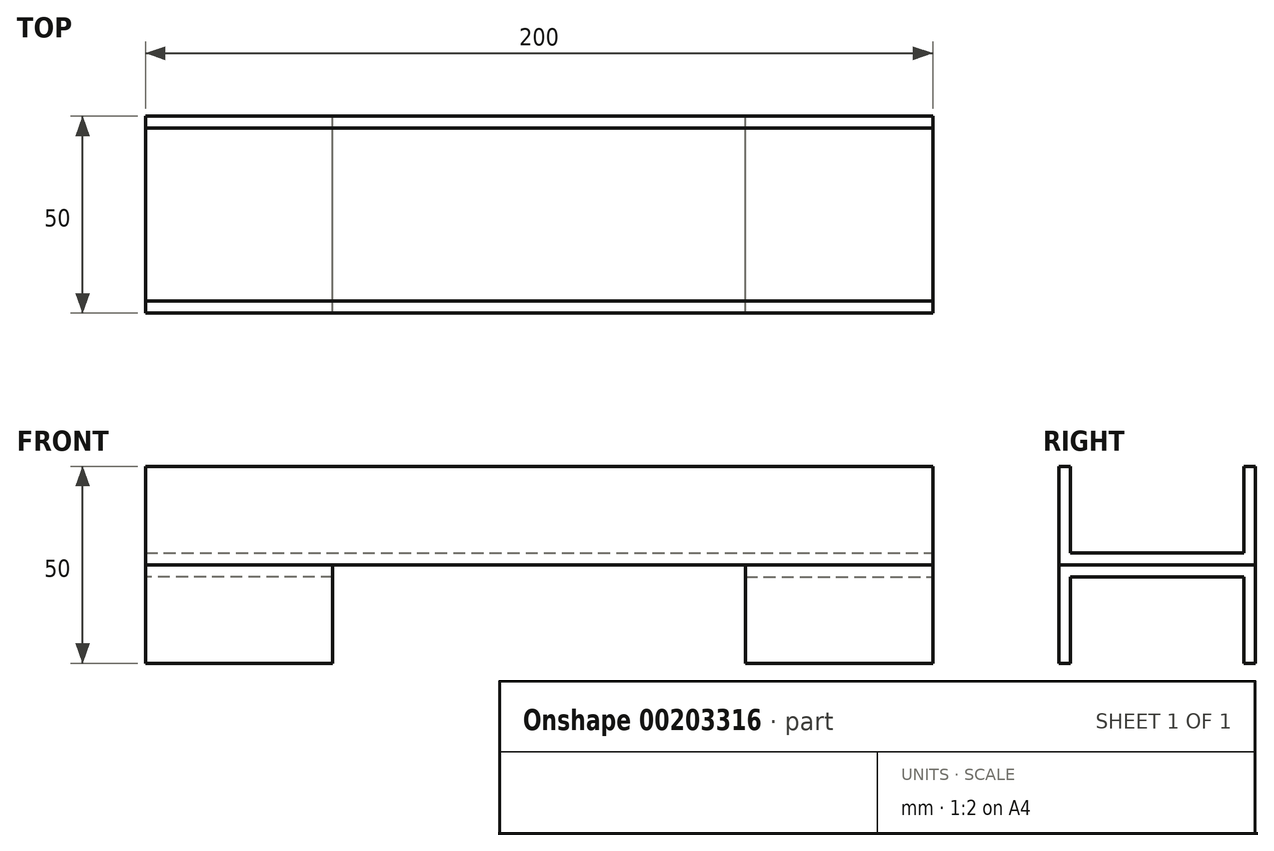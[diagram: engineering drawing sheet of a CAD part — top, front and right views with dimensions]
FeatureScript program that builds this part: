
annotation { "Feature Type Name" : "Feature", "Feature Type Description" : "" }
export const myFeature = defineFeature(function(context is Context, id is Id, definition is map)
    precondition{}
    {
        {
            var Q0;
            Q0=qCreatedBy(makeId("Front.planeOp"),FACE);
            var sketch = newSketch(context, id + "F0", { "sketchPlane" : qUnion([Q0])});
            skLineSegment(sketch, "E0.bottom", {"start": v(100, -12.5) * mm, "end": v(-100, -12.5) * mm});
            skLineSegment(sketch, "E0.top", {"start": v(100, 12.5) * mm, "end": v(-100, 12.5) * mm});
            skLineSegment(sketch, "E0.left", {"start": v(100, -12.5) * mm, "end": v(100, 12.5) * mm});
            skLineSegment(sketch, "E0.right", {"start": v(-100, -12.5) * mm, "end": v(-100, 12.5) * mm});
            skPoint(sketch, "E0.middle", {"position": v(0, 0) * mm});
            skSolve(sketch);
        }
        {
            var Q0;
            Q0 = qSketchRegion(id + "F0", true);
            extrude(context, id + "F1", {"entities" : qUnion([Q0]), "depth" : 50 * mm});
        }
        {
            var Q0;
            Q0=makeQuery(id+"F1.opExtrude","SWEPT_FACE",FACE,{"disambiguationData":[OSD([sQuery(id+"F0.wireOp",EDGE,"E0.left")])]});
            var sketch = newSketch(context, id + "F2", { "sketchPlane" : qUnion([Q0])});
            skLineSegment(sketch, "E1.bottom", {"start": v(-47, 12.5) * mm, "end": v(-3, 12.5) * mm});
            skLineSegment(sketch, "E1.top", {"start": v(-47, -9.5) * mm, "end": v(-3, -9.5) * mm});
            skLineSegment(sketch, "E1.left", {"start": v(-47, 12.5) * mm, "end": v(-47, -9.5) * mm});
            skLineSegment(sketch, "E1.right", {"start": v(-3, 12.5) * mm, "end": v(-3, -9.5) * mm});
            skLineSegment(sketch, "E2", {"start": v(-47, 6.87) * mm, "end": v(-50, 6.87) * mm, "construction": true});
            skLineSegment(sketch, "E3", {"start": v(-12.24, -9.5) * mm, "end": v(-12.24, -12.5) * mm, "construction": true});
            skLineSegment(sketch, "E4", {"start": v(-3, 5.6) * mm, "end": v(0, 5.6) * mm, "construction": true});
            skSolve(sketch);
        }
        {
            var Q0;
            Q0 = qSketchRegion(id + "F2", true);
            extrude(context, id + "F3", {"entities" : qUnion([Q0]), "operationType" : NewBodyOperationType.REMOVE, "endBound" : BoundingType.THROUGH_ALL, "oppositeDirection" : true, "depth" : 25 * mm});
        }
        {
            var Q0;
            Q0=makeQuery(id+"F1.opExtrude","SWEPT_FACE",FACE,{"disambiguationData":[OSD([sQuery(id+"F0.wireOp",EDGE,"E0.bottom")])]});
            var sketch = newSketch(context, id + "F4", { "sketchPlane" : qUnion([Q0])});
            skLineSegment(sketch, "E5.bottom", {"start": v(-100, 50) * mm, "end": v(-52.45, 50) * mm});
            skLineSegment(sketch, "E5.top", {"start": v(-100, 0) * mm, "end": v(-52.45, 0) * mm});
            skLineSegment(sketch, "E5.left", {"start": v(-100, 50) * mm, "end": v(-100, 0) * mm});
            skLineSegment(sketch, "E5.right", {"start": v(-52.45, 50) * mm, "end": v(-52.45, 0) * mm});
            skSolve(sketch);
        }
        {
            var Q0;
            Q0 = qSketchRegion(id + "F4", true);
            extrude(context, id + "F5", {"entities" : qUnion([Q0]), "depth" : 25 * mm});
        }
        {
            var Q0;
            Q0=makeQuery(id+"F5.opExtrude","SWEPT_FACE",FACE,{"disambiguationData":[OSD([sQuery(id+"F4.wireOp",EDGE,"E5.left")])]});
            var sketch = newSketch(context, id + "F6", { "sketchPlane" : qUnion([Q0])});
            skLineSegment(sketch, "E6.bottom", {"start": v(3, -37.5) * mm, "end": v(47, -37.5) * mm});
            skLineSegment(sketch, "E6.top", {"start": v(3, -15.5) * mm, "end": v(47, -15.5) * mm});
            skLineSegment(sketch, "E6.left", {"start": v(3, -37.5) * mm, "end": v(3, -15.5) * mm});
            skLineSegment(sketch, "E6.right", {"start": v(47, -37.5) * mm, "end": v(47, -15.5) * mm});
            skLineSegment(sketch, "E7", {"start": v(25, -15.5) * mm, "end": v(25, -12.5) * mm, "construction": true});
            skPoint(sketch, "E7.startSnap0", {"position": v(25, -12.5) * mm});
            skLineSegment(sketch, "E8", {"start": v(47, -26.5) * mm, "end": v(50, -26.5) * mm, "construction": true});
            skLineSegment(sketch, "E9", {"start": v(3, -26.5) * mm, "end": v(0, -26.5) * mm, "construction": true});
            skSolve(sketch);
        }
        {
            var Q0;
            Q0=makeQuery(id+"F6.imprint","IMPRINT",FACE,{"disambiguationData":[TD([[makeQuery(id+"F6.imprint","IMPRINT",EDGE,{"derivedFrom":sQuery(id+"F6.wireOp",EDGE,"E6.bottom")}),-1.0]])]});
            extrude(context, id + "F7", {"entities" : qUnion([Q0]), "operationType" : NewBodyOperationType.REMOVE, "endBound" : BoundingType.THROUGH_ALL, "oppositeDirection" : true, "depth" : 25 * mm});
        }
        {
            var Q0;
            Q0=makeQuery(id+"F5.opExtrude","SWEPT_BODY",BODY,{"disambiguationData":[OSD([sQuery(id+"F4.wireOp",EDGE,"E5.bottom"),sQuery(id+"F4.wireOp",EDGE,"E5.top"),sQuery(id+"F4.wireOp",EDGE,"E5.left"),sQuery(id+"F4.wireOp",EDGE,"E5.right")])]});
            var Q1;
            Q1=qCreatedBy(makeId("Right.planeOp"),FACE);
            mirror(context, id + "F8", {"entities" : qUnion([Q0]), "mirrorPlane" : qUnion([Q1])});
        }
    });
